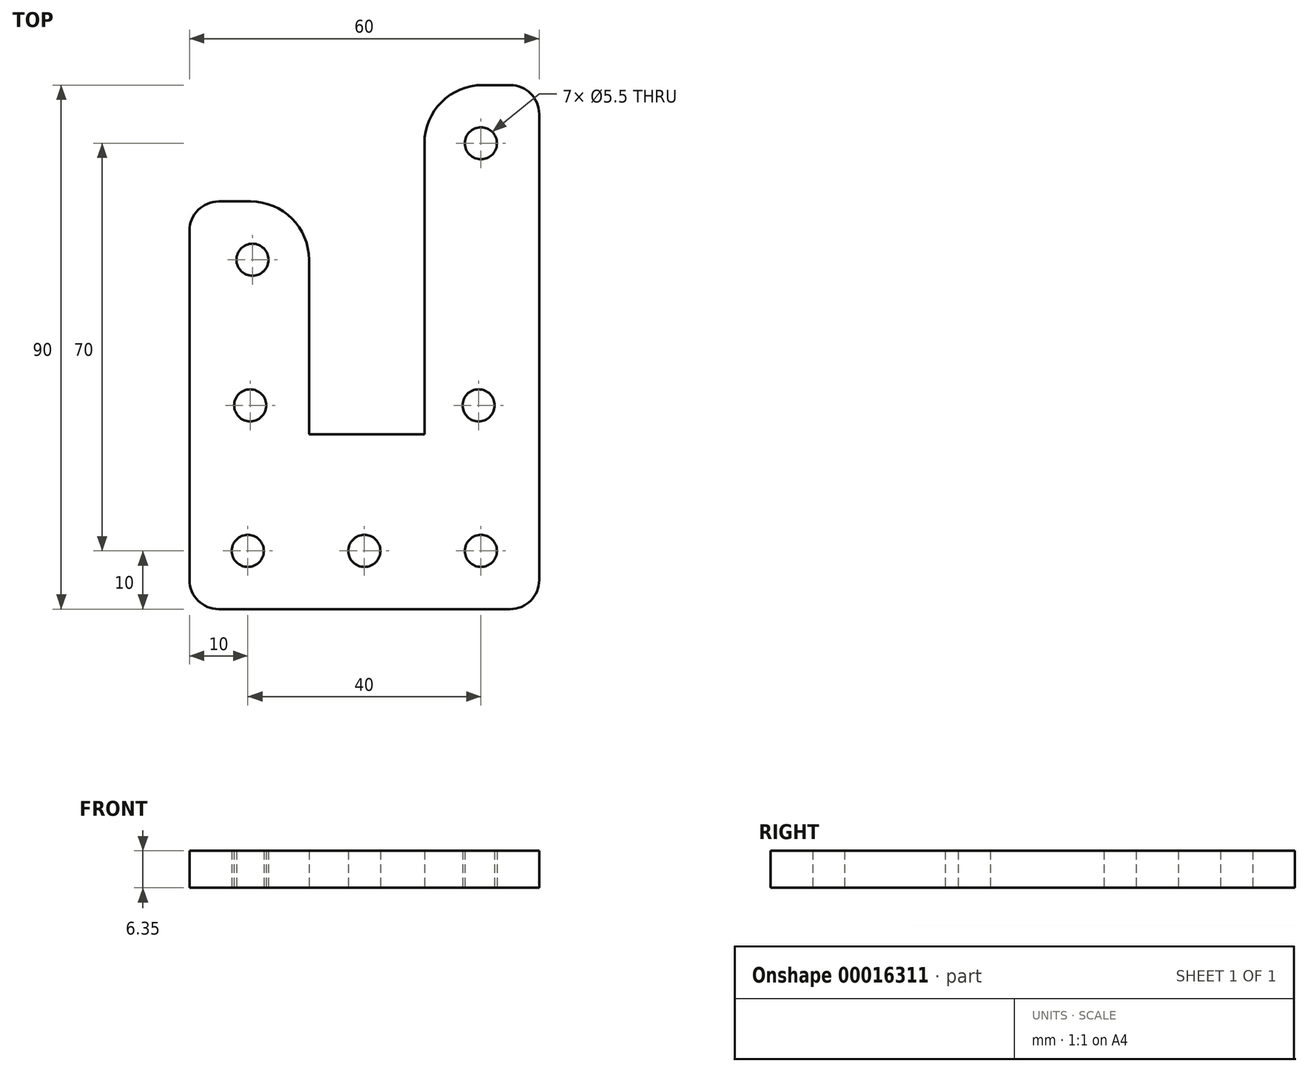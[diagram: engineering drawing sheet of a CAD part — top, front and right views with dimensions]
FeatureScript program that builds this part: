
annotation { "Feature Type Name" : "Feature", "Feature Type Description" : "" }
export const myFeature = defineFeature(function(context is Context, id is Id, definition is map)
    precondition{}
    {
        {
            var Q0;
            Q0=qCreatedBy(makeId("Top.planeOp"),FACE);
            var sketch = newSketch(context, id + "F0", { "sketchPlane" : qUnion([Q0])});
            skLineSegment(sketch, "E0.bottom", {"start": v(5, 0) * mm, "end": v(55, 0) * mm});
            skLineSegment(sketch, "E0.top", {"start": v(50.3, 90) * mm, "end": v(55, 90) * mm});
            skLineSegment(sketch, "E0.left", {"start": v(0, 5) * mm, "end": v(0, 65) * mm});
            skLineSegment(sketch, "E0.right", {"start": v(60, 5) * mm, "end": v(60, 85) * mm});
            skLineSegment(sketch, "E1.top", {"start": v(5, 70) * mm, "end": v(10.5, 70) * mm});
            skLineSegment(sketch, "E2.top", {"start": v(40.3, 30) * mm, "end": v(20.5, 30) * mm});
            skLineSegment(sketch, "E2.left", {"start": v(40.3, 80) * mm, "end": v(40.3, 30) * mm});
            skLineSegment(sketch, "E2.right", {"start": v(20.5, 60) * mm, "end": v(20.5, 30) * mm});
            skLineSegment(sketch, "E3", {"start": v(10, 0) * mm, "end": v(10, 10) * mm, "construction": true});
            skLineSegment(sketch, "E4", {"start": v(50, 0) * mm, "end": v(50, 10) * mm, "construction": true});
            skLineSegment(sketch, "E5", {"start": v(10.8, 60) * mm, "end": v(10.8, 70) * mm, "construction": true});
            skLineSegment(sketch, "E6", {"start": v(10, 10) * mm, "end": v(30, 10) * mm, "construction": true});
            skLineSegment(sketch, "E7", {"start": v(30, 10) * mm, "end": v(50, 10) * mm, "construction": true});
            skLineSegment(sketch, "E8", {"start": v(50, 10) * mm, "end": v(60, 10) * mm, "construction": true});
            skLineSegment(sketch, "E9", {"start": v(10, 10) * mm, "end": v(0, 10) * mm, "construction": true});
            skLineSegment(sketch, "E10", {"start": v(10.8, 60) * mm, "end": v(10, 10) * mm, "construction": true});
            skLineSegment(sketch, "E11", {"start": v(47.25, 30) * mm, "end": v(50, 30) * mm, "construction": true});
            skCircle(sketch, "E12", {"center": v(10.8, 60) * mm, "radius": 2.75 * mm});
            skCircle(sketch, "E13", {"center": v(50, 80) * mm, "radius": 2.75 * mm});
            skCircle(sketch, "E14", {"center": v(50, 10) * mm, "radius": 2.75 * mm});
            skCircle(sketch, "E15", {"center": v(30, 10) * mm, "radius": 2.75 * mm});
            skCircle(sketch, "E16", {"center": v(10, 10) * mm, "radius": 2.75 * mm});
            skCircle(sketch, "E17", {"center": v(10.4, 35) * mm, "radius": 2.75 * mm});
            skLineSegment(sketch, "E18", {"start": v(50, 80) * mm, "end": v(50, 90) * mm, "construction": true});
            skPoint(sketch, "E19.visualSharp", {"position": v(20.5, 70) * mm});
            skArc(sketch, "E19.filletArc", {"start": v(20.5, 60) * mm, "mid": v(17.57, 67.07) * mm, "end": v(10.5, 70) * mm});
            skPoint(sketch, "E20.visualSharp", {"position": v(0, 70) * mm});
            skArc(sketch, "E20.filletArc", {"start": v(5, 70) * mm, "mid": v(1.46, 68.54) * mm, "end": v(0, 65) * mm});
            skPoint(sketch, "E21.visualSharp", {"position": v(40.3, 90) * mm});
            skArc(sketch, "E21.filletArc", {"start": v(50.3, 90) * mm, "mid": v(43.23, 87.07) * mm, "end": v(40.3, 80) * mm});
            skPoint(sketch, "E22.visualSharp", {"position": v(60, 90) * mm});
            skArc(sketch, "E22.filletArc", {"start": v(60, 85) * mm, "mid": v(58.54, 88.54) * mm, "end": v(55, 90) * mm});
            skPoint(sketch, "E23.visualSharp", {"position": v(60, 0) * mm});
            skArc(sketch, "E23.filletArc", {"start": v(55, 0) * mm, "mid": v(58.54, 1.46) * mm, "end": v(60, 5) * mm});
            skPoint(sketch, "E24.visualSharp", {"position": v(0, 0) * mm});
            skArc(sketch, "E24.filletArc", {"start": v(0, 5) * mm, "mid": v(1.46, 1.46) * mm, "end": v(5, 0) * mm});
            skLineSegment(sketch, "E25", {"start": v(30, 0) * mm, "end": v(30, 73.01) * mm, "construction": true});
            skCircle(sketch, "E26", {"center": v(49.6, 35) * mm, "radius": 2.75 * mm});
            skSolve(sketch);
        }
        {
            var Q0;
            Q0=makeQuery(id+"F0.imprint","IMPRINT",FACE,{"disambiguationData":[TD([[makeQuery(id+"F0.imprint","IMPRINT",EDGE,{"derivedFrom":sQuery(id+"F0.wireOp",EDGE,"E0.bottom")}),1.0]])]});
            extrude(context, id + "F1", {"entities" : qUnion([Q0]), "depth" : 6.35 * mm});
        }
    });
